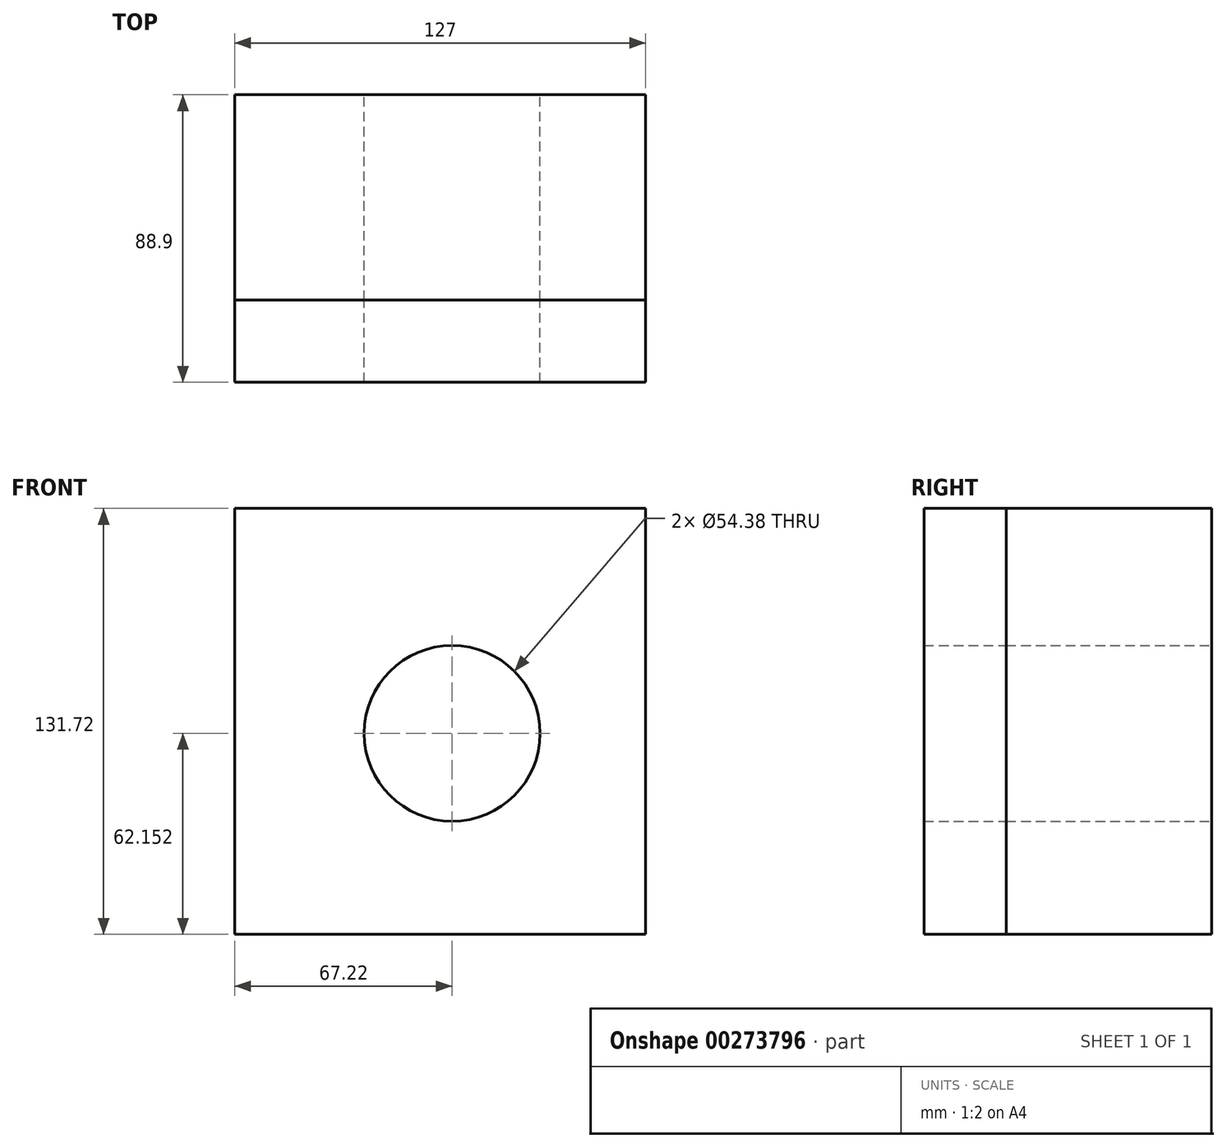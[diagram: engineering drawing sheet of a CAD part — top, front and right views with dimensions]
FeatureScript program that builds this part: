
annotation { "Feature Type Name" : "Feature", "Feature Type Description" : "" }
export const myFeature = defineFeature(function(context is Context, id is Id, definition is map)
    precondition{}
    {
        {
            var Q0;
            Q0=qCreatedBy(makeId("Front.planeOp"),FACE);
            var sketch = newSketch(context, id + "F0", { "sketchPlane" : qUnion([Q0])});
            skLineSegment(sketch, "E0.bottom", {"start": v(59.78, 65.86) * mm, "end": v(-67.22, 65.86) * mm});
            skLineSegment(sketch, "E0.top", {"start": v(59.78, -65.86) * mm, "end": v(-67.22, -65.86) * mm});
            skLineSegment(sketch, "E0.left", {"start": v(59.78, 65.86) * mm, "end": v(59.78, -65.86) * mm});
            skLineSegment(sketch, "E0.right", {"start": v(-67.22, 65.86) * mm, "end": v(-67.22, -65.86) * mm});
            skPoint(sketch, "E0.middle", {"position": v(-3.72, 0) * mm});
            skCircle(sketch, "E1", {"center": v(0, -3.7) * mm, "radius": 27.2 * mm});
            skSolve(sketch);
        }
        {
            var Q0;
            Q0=makeQuery(id+"F0.imprint","IMPRINT",FACE,{"disambiguationData":[TD([[makeQuery(id+"F0.imprint","IMPRINT",EDGE,{"derivedFrom":sQuery(id+"F0.wireOp",EDGE,"E0.bottom")}),1.0]])]});
            extrude(context, id + "F1", {"entities" : qUnion([Q0]), "depth" : 63.5 * mm});
        }
        {
            var Q0;
            Q0=makeQuery(id+"F1.opExtrude","CAP_FACE",FACE,{"disambiguationData":[OSD([sQuery(id+"F0.wireOp",EDGE,"E0.bottom"),sQuery(id+"F0.wireOp",EDGE,"E0.top"),sQuery(id+"F0.wireOp",EDGE,"E0.left"),sQuery(id+"F0.wireOp",EDGE,"E0.right"),sQuery(id+"F0.wireOp",EDGE,"E1")])],"isStart":false});
            extrude(context, id + "F2", {"entities" : qUnion([Q0]), "depth" : 25.4 * mm});
        }
    });
